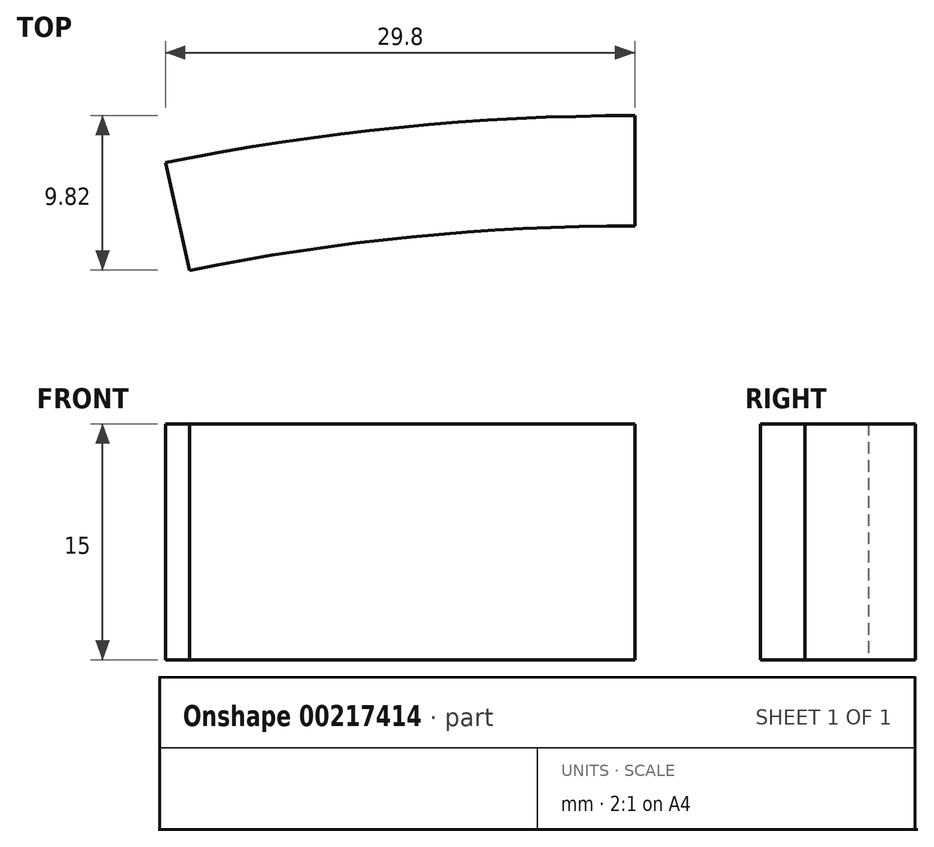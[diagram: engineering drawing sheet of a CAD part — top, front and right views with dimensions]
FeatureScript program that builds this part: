
annotation { "Feature Type Name" : "Feature", "Feature Type Description" : "" }
export const myFeature = defineFeature(function(context is Context, id is Id, definition is map)
    precondition{}
    {
        {
            var Q0;
            Q0=qCreatedBy(makeId("Top.planeOp"),FACE);
            var sketch = newSketch(context, id + "F0", { "sketchPlane" : qUnion([Q0])});
            skCircle(sketch, "E0", {"center": v(0, 0) * mm, "radius": 150 * mm, "construction": true});
            skArc(sketch, "E1", {"start": v(-29.8, 147) * mm, "mid": v(-14.98, 149.25) * mm, "end": v(0, 150) * mm});
            skArc(sketch, "E2", {"start": v(-28.28, 140.18) * mm, "mid": v(-14.2, 142.3) * mm, "end": v(0, 143) * mm});
            skLineSegment(sketch, "E3", {"start": v(0, 143) * mm, "end": v(0, 150) * mm});
            skLineSegment(sketch, "E4", {"start": v(-28.28, 140.18) * mm, "end": v(-29.8, 147) * mm});
            skSolve(sketch);
        }
        {
            var Q0;
            Q0 = qSketchRegion(id + "F0", true);
            extrude(context, id + "F1", {"entities" : qUnion([Q0]), "depth" : 15 * mm});
        }
    });
